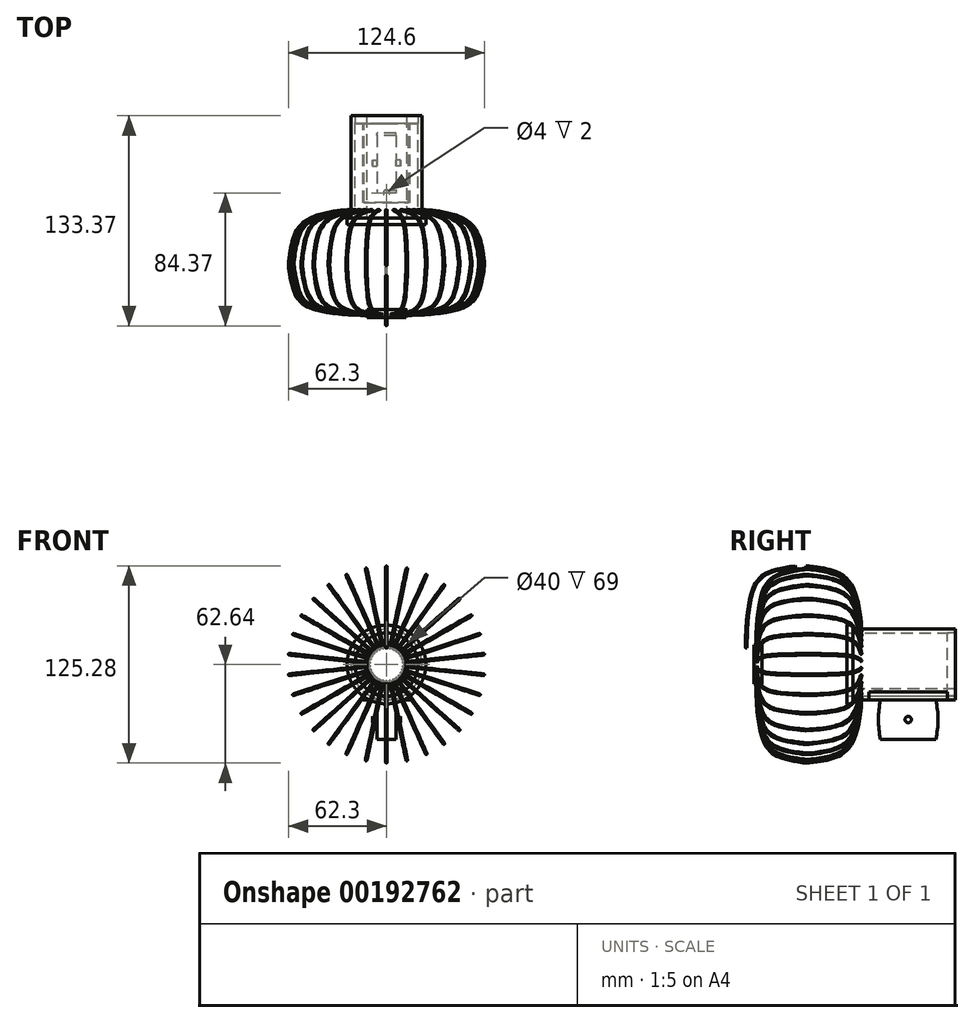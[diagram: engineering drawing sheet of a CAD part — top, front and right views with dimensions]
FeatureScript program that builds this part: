
annotation { "Feature Type Name" : "Feature", "Feature Type Description" : "" }
export const myFeature = defineFeature(function(context is Context, id is Id, definition is map)
    precondition{}
    {
        {
            var Q0;
            Q0=qCreatedBy(makeId("Right.planeOp"),FACE);
            var sketch = newSketch(context, id + "F0", { "sketchPlane" : qUnion([Q0])});
            skLineSegment(sketch, "E0.bottom", {"start": v(17.5, -12.5) * mm, "end": v(-17.5, -12.5) * mm});
            skLineSegment(sketch, "E0.top", {"start": v(17.5, 12.5) * mm, "end": v(-17.5, 12.5) * mm});
            skLineSegment(sketch, "E0.left", {"start": v(17.5, -12.5) * mm, "end": v(17.5, 12.5) * mm});
            skLineSegment(sketch, "E0.right", {"start": v(-17.5, -12.5) * mm, "end": v(-17.5, 12.5) * mm});
            skPoint(sketch, "E0.middle", {"position": v(0, 0) * mm});
            skArc(sketch, "E1", {"start": v(-17.5, 12.5) * mm, "mid": v(-18.94, 0) * mm, "end": v(-17.5, -12.5) * mm});
            skArc(sketch, "E2", {"start": v(17.5, -12.5) * mm, "mid": v(18.94, 0) * mm, "end": v(17.5, 12.5) * mm});
            skSolve(sketch);
        }
        {
            var Q0;
            Q0 = qSketchRegion(id + "F0", true);
            extrude(context, id + "F1", {"entities" : qUnion([Q0]), "depth" : 6 * mm, "hasSecondDirection" : true, "secondDirectionOppositeDirection" : true, "secondDirectionDepth" : 6 * mm});
        }
        {
            var Q0;
            Q0=makeQuery(id+"F1.opExtrude","CAP_FACE",FACE,{"disambiguationData":[OSD([sQuery(id+"F0.wireOp",EDGE,"E0.bottom"),sQuery(id+"F0.wireOp",EDGE,"E0.top"),sQuery(id+"F0.wireOp",EDGE,"E1"),sQuery(id+"F0.wireOp",EDGE,"E2")])],"isStart":true});
            var sketch = newSketch(context, id + "F2", { "sketchPlane" : qUnion([Q0])});
            skCircle(sketch, "E3", {"center": v(0, 0) * mm, "radius": 2 * mm});
            skSolve(sketch);
        }
        {
            var Q0;
            Q0 = qSketchRegion(id + "F2", true);
            extrude(context, id + "F3", {"entities" : qUnion([Q0]), "operationType" : NewBodyOperationType.ADD, "depth" : 3 * mm});
        }
        {
            var Q0;
            Q0=makeQuery(id+"F1.opExtrude","CAP_FACE",FACE,{"disambiguationData":[OSD([sQuery(id+"F0.wireOp",EDGE,"E0.bottom"),sQuery(id+"F0.wireOp",EDGE,"E0.top"),sQuery(id+"F0.wireOp",EDGE,"E1"),sQuery(id+"F0.wireOp",EDGE,"E2")])],"isStart":false});
            var sketch = newSketch(context, id + "F4", { "sketchPlane" : qUnion([Q0])});
            skCircle(sketch, "E4", {"center": v(0, 0) * mm, "radius": 2 * mm});
            skSolve(sketch);
        }
        {
            var Q0;
            Q0 = qSketchRegion(id + "F4", true);
            extrude(context, id + "F5", {"entities" : qUnion([Q0]), "operationType" : NewBodyOperationType.ADD, "depth" : 3 * mm});
        }
        {
            var Q0;
            Q0=makeQuery(id+"F1.opExtrude","SWEPT_FACE",FACE,{"disambiguationData":[OSD([sQuery(id+"F0.wireOp",EDGE,"E0.top")])]});
            var sketch = newSketch(context, id + "F6", { "sketchPlane" : qUnion([Q0])});
            skLineSegment(sketch, "E5.bottom", {"start": v(15, -25) * mm, "end": v(-15, -25) * mm});
            skLineSegment(sketch, "E5.top", {"start": v(15, 25) * mm, "end": v(-15, 25) * mm});
            skLineSegment(sketch, "E5.left", {"start": v(15, -25) * mm, "end": v(15, 25) * mm});
            skLineSegment(sketch, "E5.right", {"start": v(-15, -25) * mm, "end": v(-15, 25) * mm});
            skPoint(sketch, "E5.middle", {"position": v(0, 0) * mm});
            skSolve(sketch);
        }
        {
            var Q0;
            Q0 = qSketchRegion(id + "F6", true);
            extrude(context, id + "F7", {"entities" : qUnion([Q0]), "operationType" : NewBodyOperationType.ADD, "depth" : 5 * mm});
        }
        {
            var Q0;
            Q0=qCreatedBy(makeId("Front.planeOp"),FACE);
            var sketch = newSketch(context, id + "F8", { "sketchPlane" : qUnion([Q0])});
            skLineSegment(sketch, "E6", {"start": v(0, 0) * mm, "end": v(0, 35) * mm, "construction": true});
            skCircle(sketch, "E7", {"center": v(0, 35) * mm, "radius": 22.5 * mm});
            skSolve(sketch);
        }
        {
            var Q0;
            Q0 = qSketchRegion(id + "F8", true);
            var Q1;
            Q1=makeQuery(id+"F7.opExtrude","SWEPT_FACE",FACE,{"disambiguationData":[OSD([sQuery(id+"F6.wireOp",EDGE,"E5.bottom")])]});
            var Q2;
            Q2=makeQuery(id+"F7.opExtrude","SWEPT_FACE",FACE,{"disambiguationData":[OSD([sQuery(id+"F6.wireOp",EDGE,"E5.top")])]});
            extrude(context, id + "F9", {"entities" : qUnion([Q0]), "operationType" : NewBodyOperationType.ADD, "endBoundEntityFace" : qUnion([Q1]), "depth" : 35 * mm, "hasSecondDirection" : true, "secondDirectionOppositeDirection" : true, "secondDirectionBoundEntityFace" : qUnion([Q2]), "secondDirectionDepth" : 30 * mm});
        }
        {
            var Q0;
            Q0=makeQuery(id+"F9.opExtrude","CAP_FACE",FACE,{"disambiguationData":[OSD([sQuery(id+"F8.wireOp",EDGE,"E7")])],"isStart":false});
            var sketch = newSketch(context, id + "F10", { "sketchPlane" : qUnion([Q0])});
            skCircle(sketch, "E8", {"center": v(0, 35) * mm, "radius": 25 * mm});
            skSolve(sketch);
        }
        {
            var Q0;
            Q0 = qSketchRegion(id + "F10", true);
            extrude(context, id + "F11", {"entities" : qUnion([Q0]), "operationType" : NewBodyOperationType.ADD, "depth" : 4 * mm});
        }
        {
            var Q0;
            Q0=makeQuery(id+"F9.opExtrude","CAP_FACE",FACE,{"disambiguationData":[OSD([sQuery(id+"F8.wireOp",EDGE,"E7")])],"isStart":true});
            var sketch = newSketch(context, id + "F12", { "sketchPlane" : qUnion([Q0])});
            skCircle(sketch, "E9", {"center": v(0, 35) * mm, "radius": 20 * mm});
            skSolve(sketch);
        }
        {
            var Q0;
            Q0 = qSketchRegion(id + "F12", true);
            var Q1;
            Q1=makeQuery(id+"F9.opExtrude","CAP_FACE",FACE,{"disambiguationData":[OSD([sQuery(id+"F8.wireOp",EDGE,"E7")])],"isStart":false});
            extrude(context, id + "F13", {"entities" : qUnion([Q0]), "operationType" : NewBodyOperationType.REMOVE, "oppositeDirection" : true, "endBoundEntityFace" : qUnion([Q1]), "depth" : 75 * mm});
        }
        {
            var Q0;
            Q0=qCreatedBy(makeId("Right.planeOp"),FACE);
            var sketch = newSketch(context, id + "F14", { "sketchPlane" : qUnion([Q0])});
            skLineSegment(sketch, "E10", {"start": v(0, 0) * mm, "end": v(-65, 0) * mm, "construction": true});
            skLineSegment(sketch, "E11", {"start": v(-65, 0) * mm, "end": v(-65, 35) * mm, "construction": true});
            skSolve(sketch);
        }
        {
            var Q0;
            Q0=qCreatedBy(makeId("Right.planeOp"),FACE);
            var sketch = newSketch(context, id + "F15", { "sketchPlane" : qUnion([Q0])});
            skFitSpline(sketch, "E12", {"points": [v(-65, 97.14) * mm, v(-47.7, 94.15) * mm, v(-35.5, 84) * mm, v(-29.96, 57.55) * mm], "startDerivative": vector(33.84, -0.04) * mm, "endDerivative": vector(2, -57.16) * mm});
            skFitSpline(sketch, "E13", {"points": [v(-65, 97.14) * mm, v(-77.65, 94.8) * mm, v(-90.51, 85.84) * mm, v(-96.37, 45.43) * mm], "startDerivative": vector(-48.59, -6.35) * mm, "endDerivative": vector(-1.61, -82.54) * mm});
            skSolve(sketch);
        }
        {
            var Q0;
            Q0=sQuery(id+"F15.wireOp",EDGE,"E13");
            var Q1;
            Q1=sQuery(id+"F15.wireOp",VERTEX,"E12.start");
            cPlane(context, id + "F16", {"entities" : qUnion([Q0, Q1]), "cplaneType" : CPlaneType.CURVE_POINT, "offset" : 25 * mm, "width" : 150 * mm, "height" : 150 * mm});
        }
        {
            var Q0;
            Q0=qCreatedBy(id+"F16.planeOp",FACE);
            var sketch = newSketch(context, id + "F17", { "sketchPlane" : qUnion([Q0])});
            skCircle(sketch, "E14", {"center": v(0, 104.75) * mm, "radius": 0.5 * mm});
            skSolve(sketch);
        }
        {
            var Q0;
            Q0=makeQuery(id+"F17.imprint","IMPRINT",FACE,{"disambiguationData":[TD([[makeQuery(id+"F17.imprint","IMPRINT",EDGE,{"derivedFrom":sQuery(id+"F17.wireOp",EDGE,"E14")}),1.0]])]});
            var Q1;
            Q1=sQuery(id+"F15.wireOp",EDGE,"E12");
            sweep(context, id + "F18", {"profiles" : qUnion([Q0]), "path" : qUnion([Q1])});
        }
        {
            var Q0;
            Q0=makeQuery(id+"F17.imprint","IMPRINT",FACE,{"disambiguationData":[TD([[makeQuery(id+"F17.imprint","IMPRINT",EDGE,{"derivedFrom":sQuery(id+"F17.wireOp",EDGE,"E14")}),1.0]])]});
            var Q1;
            Q1=sQuery(id+"F15.wireOp",EDGE,"E13");
            sweep(context, id + "F19", {"profiles" : qUnion([Q0]), "path" : qUnion([Q1])});
        }
        {
            var Q0;
            Q0=qCreatedBy(makeId("Front.planeOp"),FACE);
            var sketch = newSketch(context, id + "F20", { "sketchPlane" : qUnion([Q0])});
            skCircle(sketch, "E15", {"center": v(0, 35) * mm, "radius": 7.5 * mm, "construction": true});
            skSolve(sketch);
        }
        {
            var Q0;
            Q0=makeQuery(id+"F19.opSweep","SWEPT_BODY",BODY,{"disambiguationData":[OSD([sQuery(id+"F15.wireOp",EDGE,"E13"),sQuery(id+"F17.wireOp",EDGE,"E14")])]});
            var Q1;
            Q1=makeQuery(id+"F18.opSweep","SWEPT_BODY",BODY,{"disambiguationData":[OSD([sQuery(id+"F15.wireOp",EDGE,"E12"),sQuery(id+"F17.wireOp",EDGE,"E14")])]});
            var Q2;
            Q2=sQuery(id+"F20.wireOp",EDGE,"E15");
            circularPattern(context, id + "F21", {"entities" : qUnion([Q0, Q1]), "axis" : qUnion([Q2]), "angle" : 360 * degree, "instanceCount" : 30, "equalSpace" : true});
        }
        {
            var Q0;
            Q0=qCreatedBy(makeId("Front.planeOp"),FACE);
            var sketch = newSketch(context, id + "F22", { "sketchPlane" : qUnion([Q0])});
            skCircle(sketch, "E16", {"center": v(0, 35) * mm, "radius": 12.5 * mm});
            skSolve(sketch);
        }
        {
            var Q0;
            Q0 = qSketchRegion(id + "F22", true);
            extrude(context, id + "F23", {"entities" : qUnion([Q0]), "depth" : 5 * mm});
        }
        {
            var Q0;
            Q0=makeQuery(id+"F23.opExtrude","SWEPT_BODY",BODY,{"disambiguationData":[OSD([sQuery(id+"F22.wireOp",EDGE,"E16")])]});
            transform(context, id + "F24", {"entities" : qUnion([Q0]), "transformType" : TransformType.TRANSLATION_3D, "dx" : 0 * mm, "dy" : -93 * mm, "dz" : 0 * mm, "makeCopy" : false});
        }
        {
            var Q0;
            Q0=makeQuery(id+"F19.opSweep","SWEPT_BODY",BODY,{"disambiguationData":[OSD([sQuery(id+"F15.wireOp",EDGE,"E13"),sQuery(id+"F17.wireOp",EDGE,"E14")])]});
            transform(context, id + "F25", {"entities" : qUnion([Q0]), "transformType" : TransformType.TRANSLATION_3D, "dx" : 0 * mm, "dy" : -6.5 * mm, "dz" : 0 * mm, "makeCopy" : false});
        }
        {
            var Q0;
            Q0=makeQuery(id+"F19.opSweep","SWEPT_BODY",BODY,{"disambiguationData":[OSD([sQuery(id+"F15.wireOp",EDGE,"E13"),sQuery(id+"F17.wireOp",EDGE,"E14")])]});
            var Q1;
            Q1=makeQuery(id+"F1.opExtrude","SWEPT_BODY",BODY,{"disambiguationData":[OSD([sQuery(id+"F0.wireOp",EDGE,"E0.bottom"),sQuery(id+"F0.wireOp",EDGE,"E0.top"),sQuery(id+"F0.wireOp",EDGE,"E1"),sQuery(id+"F0.wireOp",EDGE,"E2")])]});
            booleanBodies(context, id + "F26", {"operationType" : BooleanOperationType.SUBTRACTION, "tools" : qUnion([Q0]), "targets" : qUnion([Q1]), "keepTools" : true});
        }
        {
            var Q0;
            Q0=makeQuery(id+"F11.opExtrude","CAP_FACE",FACE,{"disambiguationData":[OSD([sQuery(id+"F10.wireOp",EDGE,"E8")])],"isStart":false});
            var sketch = newSketch(context, id + "F27", { "sketchPlane" : qUnion([Q0])});
            skLineSegment(sketch, "E17", {"start": v(-12.58, 19.45) * mm, "end": v(12.58, 19.45) * mm});
            skArc(sketch, "E18", {"start": v(-12.58, 19.45) * mm, "mid": v(0, 14.7) * mm, "end": v(12.58, 19.45) * mm});
            skSolve(sketch);
        }
        {
            var Q0;
            Q0 = qSketchRegion(id + "F27", true);
            var Q1;
            Q1=makeQuery(id+"F9.opExtrude","CAP_FACE",FACE,{"disambiguationData":[OSD([sQuery(id+"F8.wireOp",EDGE,"E7")])],"isStart":true});
            extrude(context, id + "F28", {"entities" : qUnion([Q0]), "endBound" : BoundingType.UP_TO_SURFACE, "oppositeDirection" : true, "endBoundEntityFace" : qUnion([Q1]), "depth" : 25 * mm});
        }
        {
            var Q0;
            Q0=makeQuery(id+"F28.opExtrude","SWEPT_FACE",FACE,{"disambiguationData":[OSD([sQuery(id+"F27.wireOp",EDGE,"E17")])]});
            var sketch = newSketch(context, id + "F29", { "sketchPlane" : qUnion([Q0])});
            skCircle(sketch, "E19", {"center": v(0, -19) * mm, "radius": 2 * mm});
            skSolve(sketch);
        }
        {
            var Q0;
            Q0 = qSketchRegion(id + "F29", true);
            extrude(context, id + "F30", {"entities" : qUnion([Q0]), "operationType" : NewBodyOperationType.REMOVE, "oppositeDirection" : true, "depth" : 2 * mm});
        }
        {
            var Q0;
            Q0=qCreatedBy(makeId("Front.planeOp"),FACE);
            var sketch = newSketch(context, id + "F31", { "sketchPlane" : qUnion([Q0])});
            skCircle(sketch, "E20", {"center": v(0, 35) * mm, "radius": 20 * mm});
            skSolve(sketch);
        }
        {
            var Q0;
            Q0 = qSketchRegion(id + "F31", true);
            extrude(context, id + "F32", {"entities" : qUnion([Q0]), "oppositeDirection" : true, "depth" : 5 * mm});
        }
        {
            var Q0;
            Q0=makeQuery(id+"F32.opExtrude","SWEPT_BODY",BODY,{"disambiguationData":[OSD([sQuery(id+"F31.wireOp",EDGE,"E20")])]});
            transform(context, id + "F33", {"entities" : qUnion([Q0]), "transformType" : TransformType.TRANSLATION_3D, "dx" : 0 * mm, "dy" : 25 * mm, "dz" : 0 * mm, "makeCopy" : false});
        }
        {
            var Q0;
            Q0=makeQuery(id+"F1.opExtrude","SWEPT_BODY",BODY,{"disambiguationData":[OSD([sQuery(id+"F0.wireOp",EDGE,"E0.bottom"),sQuery(id+"F0.wireOp",EDGE,"E0.top"),sQuery(id+"F0.wireOp",EDGE,"E1"),sQuery(id+"F0.wireOp",EDGE,"E2")])]});
            var Q1;
            Q1=makeQuery(id+"F32.opExtrude","SWEPT_BODY",BODY,{"disambiguationData":[OSD([sQuery(id+"F31.wireOp",EDGE,"E20")])]});
            booleanBodies(context, id + "F34", {"operationType" : BooleanOperationType.SUBTRACTION, "tools" : qUnion([Q0]), "targets" : qUnion([Q1]), "keepTools" : true});
        }
    });
